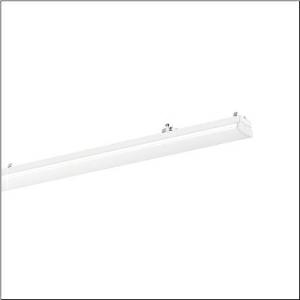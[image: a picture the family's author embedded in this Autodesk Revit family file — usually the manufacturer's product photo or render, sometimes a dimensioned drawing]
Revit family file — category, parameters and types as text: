
# Revit family: licross_r__21_recessed_opal_mo_52tl1dmn4axg_843c
name_source: partatom
category: Lighting Fixtures
units: mm (PartAtom-declared; Revit-internal decimal feet)

## family parameters
Cut with Voids When Loaded = No
Host = Face
Light Source = No
Part Type = Normal
Room Calculation Point = No
Round Connector Dimension = Use Diameter
Shared = No

## types (1)
- --- (1 x LED, 10420 lm, 60.5 W, 4000K)
    Apparent Load = 61 VA
    CIE Flux Codes = 44 73 91 87 100
    Color Rendering = 80
    Color Temperature = 4000K
    Default Elevation = 1800 mm
    Description = Licross® 21 recessed opal MO, luminaire insert, of sheet steel, galvanised, coil coated, white, length: 1.500mm, width: 66mm, height: 67mm, LED rated luminous flux: 10.420lm, light colour: 840, control gear: ON/OFF Multilumen, with plug, 3-pole, with phase selection, mains connection: 220..240V, AC, 50/60Hz, rated input power: 61W, internal wiring halogen-free, primary optical cover: cover, of PMMA, light emission: direct with ceiling illumination distribution, primary light characteristic: symmetric, protection rating (complete): IP40, insulation class (complete): insulation class I (protective earthing), certification: CE, ENEC, VDE, UKCA, protection symbol: D if used in an environment without relevant dust loads with corresponding accessories, impact resistance: IK06, permissible ambient temperature for indoor applications: -35..+40°C, corresponds to IFS (International Featured Standards) requirements for safety and quality in the food industry, reducing of maximum allowable ambient temperature of 5°C with ceiling mounting, LABS conformity tested according to VDMA 24364:2018-05, packaging unit: 1 piece
    Height = 83 mm
    Lamp = 1 x LED
    Lamp Light Flux = 10420 lm
    Lamp Power = 60.5 W
    Lamp count = 1
    Length = 1500 mm
    Luminous efficacy = 172 lm/W
    Manufacturer = Siteco
    ModVariant = No
    Model = 52TL1DMN4AXG
    Mounting Place = Ceiling
    Mounting Type = Pendant
    Number of Poles = 1
    OnlyDefault = Yes
    Power Factor = 1
    Product Name = Licross® 21 recessed opal MO
    Product group = luminaire insert | ceiling pendant
    ProductGroupID = 902
    Protection Class = Protection class I
    Protection Degree = IP 40
    RLX_Detail_Level = 1
    RLX_Emergency_Light_Flux = 0 lm
    RLX_Emergency_Type = 0
    RLX_Emergency_Type_DB = No
    RlxData = <blob elided: 24777 chars, md5=caf04c86>
    Socket = socket
    Standby Power = 0 W
    System Light Flux = 10420 lm
    System Power = 61 W
    Type Comments = factory setting: luminous flux: 100 % | (A | C | E) | 140 mA
    Type Image = l_1313666.jpg
    URL = http://relux.com
    VarID = @adj_086069
    Voltage = 0 V
    Weight = 0.00 kg
    Width = 76 mm

## geometry (parser evidence)
native form markers: Blend x4, Sweep x14
no freeform markers — native parametric forms only
